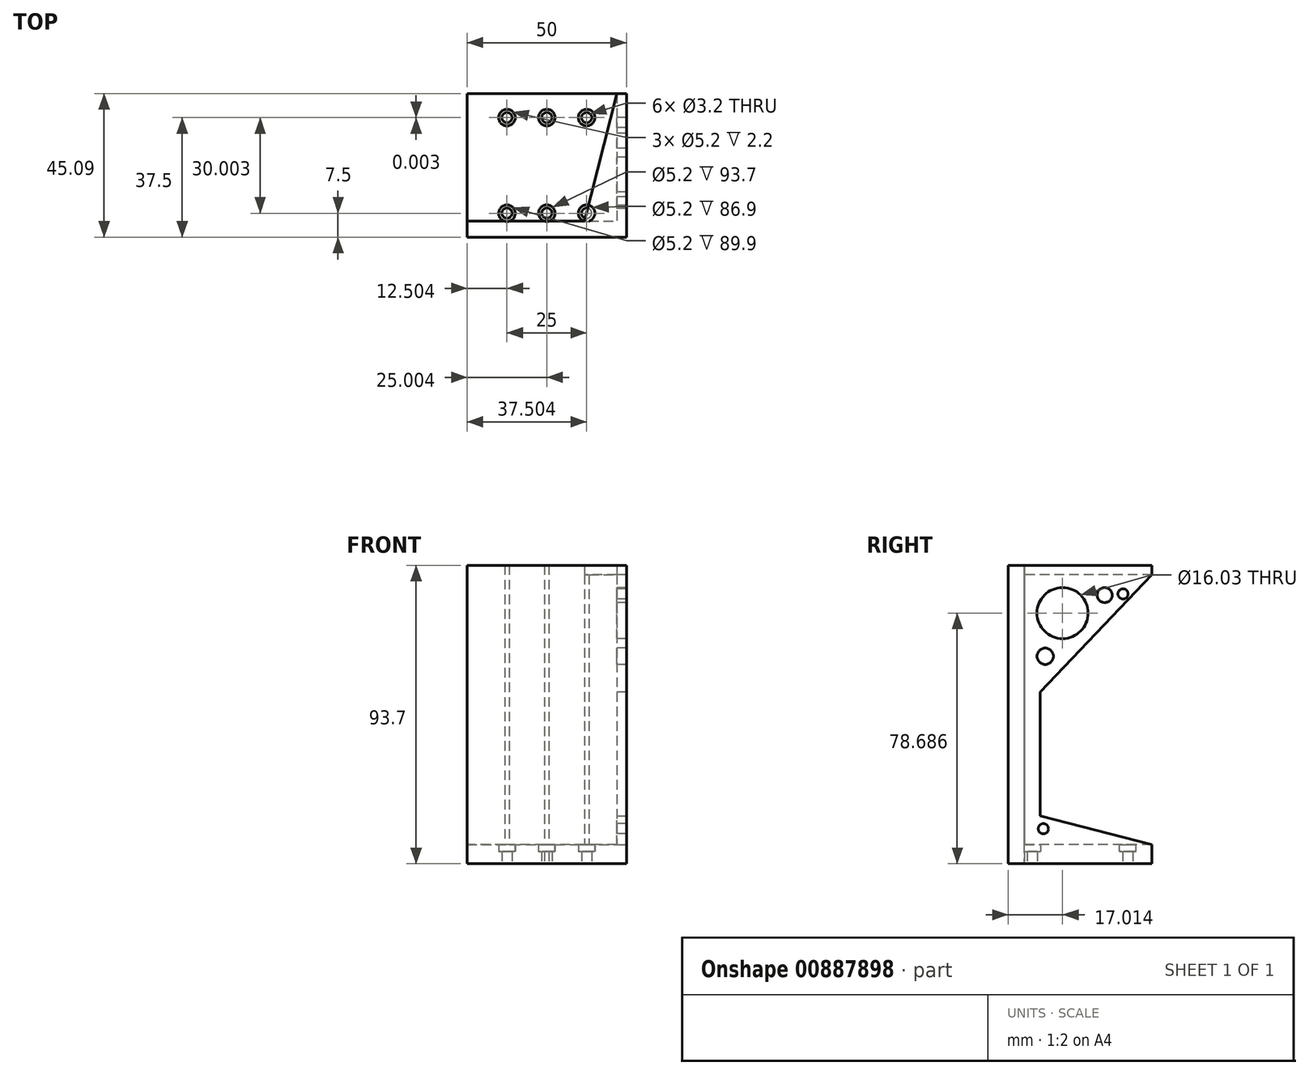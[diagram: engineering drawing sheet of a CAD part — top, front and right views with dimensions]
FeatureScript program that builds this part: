
annotation { "Feature Type Name" : "Feature", "Feature Type Description" : "" }
export const myFeature = defineFeature(function(context is Context, id is Id, definition is map)
    precondition{}
    {
        {
            assignVariable(context, id + "F0", {"name" : "pad", "anyValue" : .2});
        }
        {
            var Q0;
            Q0=qCreatedBy(makeId("Top.planeOp"),FACE);
            var sketch = newSketch(context, id + "F1", { "sketchPlane" : qUnion([Q0])});
            skLineSegment(sketch, "E0.bottom", {"start": v(-37.95, 45) * mm, "end": v(12.05, 45) * mm});
            skLineSegment(sketch, "E0.top", {"start": v(-37.95, 0) * mm, "end": v(12.05, 0) * mm});
            skLineSegment(sketch, "E0.left", {"start": v(-37.95, 45) * mm, "end": v(-37.95, 0) * mm});
            skLineSegment(sketch, "E0.right", {"start": v(12.05, 45) * mm, "end": v(12.05, 0) * mm});
            skLineSegment(sketch, "E1", {"start": v(-37.95, 5) * mm, "end": v(12.05, 5) * mm});
            skLineSegment(sketch, "E2", {"start": v(-37.95, 15) * mm, "end": v(12.05, 15) * mm, "construction": true});
            skLineSegment(sketch, "E3", {"start": v(-37.95, 7.5) * mm, "end": v(12.05, 7.5) * mm, "construction": true});
            skCircle(sketch, "E4", {"center": v(-12.95, 7.5) * mm, "radius": 1.6 * mm});
            skCircle(sketch, "E5", {"center": v(-25.45, 7.5) * mm, "radius": 1.6 * mm});
            skCircle(sketch, "E6", {"center": v(-0.45, 7.5) * mm, "radius": 1.6 * mm});
            skLineSegment(sketch, "E7", {"start": v(9.05, 45) * mm, "end": v(9.05, 0) * mm});
            skCircle(sketch, "E8", {"center": v(-25.45, 7.5) * mm, "radius": 2.6 * mm});
            skCircle(sketch, "E9", {"center": v(-12.95, 7.5) * mm, "radius": 2.6 * mm});
            skCircle(sketch, "E10", {"center": v(-0.45, 7.5) * mm, "radius": 2.6 * mm});
            skLineSegment(sketch, "E11", {"start": v(-37.95, 37.5) * mm, "end": v(12.05, 37.5) * mm, "construction": true});
            skCircle(sketch, "E12", {"center": v(-12.95, 37.5) * mm, "radius": 1.6 * mm});
            skCircle(sketch, "E13", {"center": v(-25.45, 37.5) * mm, "radius": 1.6 * mm});
            skCircle(sketch, "E14", {"center": v(-0.45, 37.5) * mm, "radius": 1.6 * mm});
            skCircle(sketch, "E15", {"center": v(-25.45, 37.5) * mm, "radius": 2.6 * mm});
            skCircle(sketch, "E16", {"center": v(-12.95, 37.5) * mm, "radius": 2.6 * mm});
            skCircle(sketch, "E17", {"center": v(-0.45, 37.5) * mm, "radius": 2.6 * mm});
            skSolve(sketch);
        }
        {
            var Q0;
            {var subQ1=sQuery(id+"F1.wireOp",EDGE,"E0.left");var subQ6=sQuery(id+"F1.wireOp",EDGE,"E0.bottom");var subQ9=makeQuery(id+"F1.imprint","INTERSECT",VERTEX,{"derivedFrom":[subQ6,subQ1]});Q0=makeQuery(id+"F1.imprint","IMPRINT",FACE,{"disambiguationData":[TD([[makeQuery(id+"F1.imprint","IMPRINT",EDGE,{"disambiguationData":[TD([[subQ9,-1.0]])],"derivedFrom":subQ6}),-1.0]])]});}
            var Q1;
            Q1=makeQuery(id+"F1.imprint","IMPRINT",FACE,{"disambiguationData":[TD([[makeQuery(id+"F1.imprint","IMPRINT",EDGE,{"derivedFrom":sQuery(id+"F1.wireOp",EDGE,"E4")}),-1.0]])]});
            var Q2;
            Q2=makeQuery(id+"F1.imprint","IMPRINT",FACE,{"disambiguationData":[TD([[makeQuery(id+"F1.imprint","IMPRINT",EDGE,{"derivedFrom":sQuery(id+"F1.wireOp",EDGE,"E6")}),-1.0]])]});
            var Q3;
            Q3=makeQuery(id+"F1.imprint","IMPRINT",FACE,{"disambiguationData":[TD([[makeQuery(id+"F1.imprint","IMPRINT",EDGE,{"derivedFrom":sQuery(id+"F1.wireOp",EDGE,"E5")}),-1.0]])]});
            var Q4;
            {var subQ0=sQuery(id+"F1.wireOp",EDGE,"E10");var subQ1=sQuery(id+"F1.wireOp",EDGE,"E1");var subQ2=makeQuery(id+"F1.imprint","INTERSECT",VERTEX,{"disambiguationData":[OD(0.0)],"derivedFrom":[subQ1,subQ0]});Q4=makeQuery(id+"F1.imprint","IMPRINT",FACE,{"disambiguationData":[TD([[makeQuery(id+"F1.imprint","IMPRINT",EDGE,{"disambiguationData":[TD([[subQ2,-1.0]])],"derivedFrom":subQ1}),-1.0]])]});}
            var Q5;
            {var subQ0=sQuery(id+"F1.wireOp",EDGE,"E9");var subQ1=sQuery(id+"F1.wireOp",EDGE,"E1");var subQ2=makeQuery(id+"F1.imprint","INTERSECT",VERTEX,{"disambiguationData":[OD(0.0)],"derivedFrom":[subQ1,subQ0]});Q5=makeQuery(id+"F1.imprint","IMPRINT",FACE,{"disambiguationData":[TD([[makeQuery(id+"F1.imprint","IMPRINT",EDGE,{"disambiguationData":[TD([[subQ2,-1.0]])],"derivedFrom":subQ1}),-1.0]])]});}
            var Q6;
            {var subQ0=sQuery(id+"F1.wireOp",EDGE,"E8");var subQ1=sQuery(id+"F1.wireOp",EDGE,"E1");var subQ2=makeQuery(id+"F1.imprint","INTERSECT",VERTEX,{"disambiguationData":[OD(0.0)],"derivedFrom":[subQ1,subQ0]});Q6=makeQuery(id+"F1.imprint","IMPRINT",FACE,{"disambiguationData":[TD([[makeQuery(id+"F1.imprint","IMPRINT",EDGE,{"disambiguationData":[TD([[subQ2,-1.0]])],"derivedFrom":subQ1}),-1.0]])]});}
            var Q7;
            Q7=makeQuery(id+"F1.imprint","IMPRINT",FACE,{"disambiguationData":[TD([[makeQuery(id+"F1.imprint","IMPRINT",EDGE,{"derivedFrom":sQuery(id+"F1.wireOp",EDGE,"E13")}),-1.0]])]});
            var Q8;
            Q8=makeQuery(id+"F1.imprint","IMPRINT",FACE,{"disambiguationData":[TD([[makeQuery(id+"F1.imprint","IMPRINT",EDGE,{"derivedFrom":sQuery(id+"F1.wireOp",EDGE,"E12")}),-1.0]])]});
            var Q9;
            Q9=makeQuery(id+"F1.imprint","IMPRINT",FACE,{"disambiguationData":[TD([[makeQuery(id+"F1.imprint","IMPRINT",EDGE,{"derivedFrom":sQuery(id+"F1.wireOp",EDGE,"E14")}),-1.0]])]});
            extrude(context, id + "F2", {"entities" : qUnion([Q0, Q1, Q2, Q3, Q4, Q5, Q6, Q7, Q8, Q9]), "depth" : (4 + 2) * mm, "offsetDistance" : 25 * mm});
        }
        {
            var Q0;
            {var subQ0=sQuery(id+"F1.wireOp",EDGE,"E0.left");var subQ1=sQuery(id+"F1.wireOp",EDGE,"E0.top");var subQ2=makeQuery(id+"F1.imprint","INTERSECT",VERTEX,{"derivedFrom":[subQ1,subQ0]});Q0=makeQuery(id+"F1.imprint","IMPRINT",FACE,{"disambiguationData":[TD([[makeQuery(id+"F1.imprint","IMPRINT",EDGE,{"disambiguationData":[TD([[subQ2,-1.0]])],"derivedFrom":subQ1}),1.0]])]});}
            var Q1;
            {var subQ0=sQuery(id+"F1.wireOp",EDGE,"E0.right");var subQ1=sQuery(id+"F1.wireOp",EDGE,"E0.top");var subQ2=makeQuery(id+"F1.imprint","INTERSECT",VERTEX,{"derivedFrom":[subQ1,subQ0]});Q1=makeQuery(id+"F1.imprint","IMPRINT",FACE,{"disambiguationData":[TD([[makeQuery(id+"F1.imprint","IMPRINT",EDGE,{"disambiguationData":[TD([[subQ2,1.0]])],"derivedFrom":subQ1}),1.0]])]});}
            var Q2;
            Q2=makeQuery(id+"F2.opExtrude","CAP_FACE",FACE,{"disambiguationData":[OSD([sQuery(id+"F1.wireOp",EDGE,"E0.bottom"),sQuery(id+"F1.wireOp",EDGE,"E0.left"),sQuery(id+"F1.wireOp",EDGE,"E1"),sQuery(id+"F1.wireOp",EDGE,"E4"),sQuery(id+"F1.wireOp",EDGE,"E5"),sQuery(id+"F1.wireOp",EDGE,"E6"),sQuery(id+"F1.wireOp",EDGE,"E7"),sQuery(id+"F1.wireOp",EDGE,"E8"),sQuery(id+"F1.wireOp",EDGE,"E9"),sQuery(id+"F1.wireOp",EDGE,"E10")])],"isStart":false});
            extrude(context, id + "F3", {"entities" : qUnion([Q0, Q1]), "operationType" : NewBodyOperationType.ADD, "endBound" : BoundingType.UP_TO_SURFACE, "depth" : 50 * mm, "endBoundEntityFace" : qUnion([Q2]), "hasOffset" : true, "offsetDistance" : (84.5 + getVariable(context, 'pad')) * mm, "offsetOppositeDirection" : true});
        }
        {
            var Q0;
            {var subQ0=sQuery(id+"F1.wireOp",EDGE,"E0.right");var subQ1=sQuery(id+"F1.wireOp",EDGE,"E0.bottom");var subQ2=makeQuery(id+"F1.imprint","INTERSECT",VERTEX,{"derivedFrom":[subQ1,subQ0]});Q0=makeQuery(id+"F1.imprint","IMPRINT",FACE,{"disambiguationData":[TD([[makeQuery(id+"F1.imprint","IMPRINT",EDGE,{"disambiguationData":[TD([[subQ2,1.0]])],"derivedFrom":subQ1}),-1.0]])]});}
            var Q1;
            Q1=makeQuery(id+"F2.opExtrude","CAP_FACE",FACE,{"disambiguationData":[OSD([sQuery(id+"F1.wireOp",EDGE,"E0.bottom"),sQuery(id+"F1.wireOp",EDGE,"E0.left"),sQuery(id+"F1.wireOp",EDGE,"E1"),sQuery(id+"F1.wireOp",EDGE,"E4"),sQuery(id+"F1.wireOp",EDGE,"E5"),sQuery(id+"F1.wireOp",EDGE,"E6"),sQuery(id+"F1.wireOp",EDGE,"E7")])],"isStart":false});
            extrude(context, id + "F4", {"entities" : qUnion([Q0]), "operationType" : NewBodyOperationType.ADD, "endBound" : BoundingType.UP_TO_SURFACE, "depth" : 25 * mm, "endBoundEntityFace" : qUnion([Q1]), "hasOffset" : true, "offsetDistance" : 9 * mm, "offsetOppositeDirection" : true});
        }
        {
            var Q0;
            Q0=makeQuery(id+"F2.opExtrude","CAP_FACE",FACE,{"disambiguationData":[OSD([sQuery(id+"F1.wireOp",EDGE,"E0.bottom"),sQuery(id+"F1.wireOp",EDGE,"E0.left"),sQuery(id+"F1.wireOp",EDGE,"E1"),sQuery(id+"F1.wireOp",EDGE,"E4"),sQuery(id+"F1.wireOp",EDGE,"E5"),sQuery(id+"F1.wireOp",EDGE,"E6"),sQuery(id+"F1.wireOp",EDGE,"E7")])],"isStart":false});
            var sketch = newSketch(context, id + "F5", { "sketchPlane" : qUnion([Q0])});
            skCircle(sketch, "E18.0", {"center": v(-25.45, 7.5) * mm, "radius": 2.6 * mm});
            skCircle(sketch, "E19.0", {"center": v(-12.95, 7.5) * mm, "radius": 2.6 * mm});
            skCircle(sketch, "E20.0", {"center": v(-0.45, 7.5) * mm, "radius": 2.6 * mm});
            skCircle(sketch, "E21.0", {"center": v(-25.45, 37.5) * mm, "radius": 2.6 * mm});
            skCircle(sketch, "E22.0", {"center": v(-12.95, 37.5) * mm, "radius": 2.6 * mm});
            skCircle(sketch, "E23.0", {"center": v(-0.45, 37.5) * mm, "radius": 2.6 * mm});
            skSolve(sketch);
        }
        {
            var Q0;
            {var subQ7=sQuery(id+"F1.wireOp",EDGE,"E5");Q0=makeQuery(id+"F5.imprint","IMPRINT",FACE,{"disambiguationData":[TD([[makeQuery(id+"F5.imprint","IMPRINT",EDGE,{"derivedFrom":makeQuery(id+"F2.opExtrude","CAP_EDGE",EDGE,{"disambiguationData":[OSD([subQ7])],"isStart":false})}),-1.0]])]});}
            var Q1;
            {var subQ6=sQuery(id+"F1.wireOp",EDGE,"E4");Q1=makeQuery(id+"F5.imprint","IMPRINT",FACE,{"disambiguationData":[TD([[makeQuery(id+"F5.imprint","IMPRINT",EDGE,{"derivedFrom":makeQuery(id+"F2.opExtrude","CAP_EDGE",EDGE,{"disambiguationData":[OSD([subQ6])],"isStart":false})}),-1.0]])]});}
            var Q2;
            {var subQ8=sQuery(id+"F1.wireOp",EDGE,"E6");Q2=makeQuery(id+"F5.imprint","IMPRINT",FACE,{"disambiguationData":[TD([[makeQuery(id+"F5.imprint","IMPRINT",EDGE,{"derivedFrom":makeQuery(id+"F2.opExtrude","CAP_EDGE",EDGE,{"disambiguationData":[OSD([subQ8])],"isStart":false})}),-1.0]])]});}
            var Q3;
            Q3=makeQuery(id+"F5.imprint","IMPRINT",FACE,{"disambiguationData":[TD([[makeQuery(id+"F5.imprint","IMPRINT",EDGE,{"derivedFrom":sQuery(id+"F5.wireOp",EDGE,"E21.0")}),1.0]])]});
            var Q4;
            Q4=makeQuery(id+"F5.imprint","IMPRINT",FACE,{"disambiguationData":[TD([[makeQuery(id+"F5.imprint","IMPRINT",EDGE,{"derivedFrom":sQuery(id+"F5.wireOp",EDGE,"E22.0")}),1.0]])]});
            var Q5;
            Q5=makeQuery(id+"F5.imprint","IMPRINT",FACE,{"disambiguationData":[TD([[makeQuery(id+"F5.imprint","IMPRINT",EDGE,{"derivedFrom":sQuery(id+"F5.wireOp",EDGE,"E23.0")}),1.0]])]});
            extrude(context, id + "F6", {"entities" : qUnion([Q0, Q1, Q2, Q3, Q4, Q5]), "operationType" : NewBodyOperationType.REMOVE, "oppositeDirection" : true, "depth" : (2 + getVariable(context, 'pad')) * mm, "offsetDistance" : 25 * mm});
        }
        {
            var Q0;
            Q0=makeQuery(id+"F4.opExtrude","CAP_FACE",FACE,{"disambiguationData":[OSD([sQuery(id+"F1.wireOp",EDGE,"E0.bottom"),sQuery(id+"F1.wireOp",EDGE,"E0.right"),sQuery(id+"F1.wireOp",EDGE,"E1"),sQuery(id+"F1.wireOp",EDGE,"E7")])],"isStart":false});
            var sketch = newSketch(context, id + "F7", { "sketchPlane" : qUnion([Q0])});
            skLineSegment(sketch, "E24", {"start": v(9.05, 10) * mm, "end": v(12.05, 10) * mm});
            skSolve(sketch);
        }
        {
            var Q0;
            {var subQ0=sQuery(id+"F7.wireOp",EDGE,"E24");Q0=makeQuery(id+"F7.imprint","IMPRINT",FACE,{"disambiguationData":[TD([[makeQuery(id+"F7.imprint","IMPRINT",EDGE,{"derivedFrom":subQ0}),-1.0]])]});}
            var Q1;
            Q1=makeQuery(id+"F3.opExtrude","CAP_FACE",FACE,{"disambiguationData":[OSD([sQuery(id+"F1.wireOp",EDGE,"E0.top"),sQuery(id+"F1.wireOp",EDGE,"E0.left"),sQuery(id+"F1.wireOp",EDGE,"E0.right"),sQuery(id+"F1.wireOp",EDGE,"E1"),sQuery(id+"F1.wireOp",EDGE,"E8"),sQuery(id+"F1.wireOp",EDGE,"E9"),sQuery(id+"F1.wireOp",EDGE,"E10")])],"isStart":false});
            extrude(context, id + "F8", {"entities" : qUnion([Q0]), "operationType" : NewBodyOperationType.ADD, "endBound" : BoundingType.UP_TO_SURFACE, "depth" : 25 * mm, "endBoundEntityFace" : qUnion([Q1]), "offsetDistance" : 25 * mm});
        }
        {
            var Q0;
            {var subQ0=sQuery(id+"F1.wireOp",EDGE,"E7");Q0=makeQuery(id+"F8.boolean.opBoolean","MERGE",FACE,{"derivedFrom":[makeQuery(id+"F4.opExtrude","SWEPT_FACE",FACE,{"disambiguationData":[OSD([subQ0])]}),makeQuery(id+"F8.opExtrude","SWEPT_FACE",FACE,{"disambiguationData":[OSD([subQ0])]})]});}
            var sketch = newSketch(context, id + "F9", { "sketchPlane" : qUnion([Q0])});
            skLineSegment(sketch, "E25", {"start": v(-45.1, 90.7) * mm, "end": v(-5, 48.7) * mm});
            skLineSegment(sketch, "E26", {"start": v(-45.1, 90.7) * mm, "end": v(-5, 90.7) * mm});
            skSolve(sketch);
        }
        {
            var Q0;
            {var subQ0=sQuery(id+"F9.wireOp",EDGE,"E26");var subQ1=sQuery(id+"F9.wireOp",EDGE,"E25");var subQ2=makeQuery(id+"F9.imprint","INTERSECT",VERTEX,{"derivedFrom":[subQ1,subQ0]});Q0=makeQuery(id+"F9.imprint","IMPRINT",FACE,{"disambiguationData":[TD([[makeQuery(id+"F9.imprint","IMPRINT",EDGE,{"disambiguationData":[TD([[subQ2,-1.0]])],"derivedFrom":subQ1}),1.0]])]});}
            var Q1;
            {var subQ0=sQuery(id+"F1.wireOp",EDGE,"E0.right");Q1=makeQuery(id+"F12.boolean.opBoolean","MERGE",FACE,{"derivedFrom":[makeQuery(id+"F8.boolean.opBoolean","MERGE",FACE,{"derivedFrom":[makeQuery(id+"F4.boolean.opBoolean","MERGE",FACE,{"derivedFrom":[makeQuery(id+"F3.opExtrude","SWEPT_FACE",FACE,{"disambiguationData":[OSD([subQ0])]}),makeQuery(id+"F4.opExtrude","SWEPT_FACE",FACE,{"disambiguationData":[OSD([subQ0])]})]}),makeQuery(id+"F8.opExtrude","SWEPT_FACE",FACE,{"disambiguationData":[OSD([subQ0])]})]}),makeQuery(id+"F12.opExtrude","SWEPT_FACE",FACE,{"disambiguationData":[OSD([subQ0])]})]});}
            extrude(context, id + "F10", {"entities" : qUnion([Q0]), "operationType" : NewBodyOperationType.ADD, "endBound" : BoundingType.UP_TO_SURFACE, "oppositeDirection" : true, "depth" : 25 * mm, "endBoundEntityFace" : qUnion([Q1]), "offsetDistance" : 25 * mm});
        }
        {
            var Q0;
            {var subQ0=sQuery(id+"F1.wireOp",EDGE,"E1");var subQ1=sQuery(id+"F1.wireOp",EDGE,"E0.right");Q0=makeQuery(id+"F8.boolean.opBoolean","MERGE",FACE,{"derivedFrom":[makeQuery(id+"F3.opExtrude","CAP_FACE",FACE,{"disambiguationData":[OSD([sQuery(id+"F1.wireOp",EDGE,"E0.top"),sQuery(id+"F1.wireOp",EDGE,"E0.left"),subQ1,subQ0,sQuery(id+"F1.wireOp",EDGE,"E8"),sQuery(id+"F1.wireOp",EDGE,"E9"),sQuery(id+"F1.wireOp",EDGE,"E10")])],"isStart":false}),makeQuery(id+"F8.opExtrude","CAP_FACE",FACE,{"disambiguationData":[OSD([subQ1,subQ0,sQuery(id+"F1.wireOp",EDGE,"E7"),sQuery(id+"F7.wireOp",EDGE,"E24")])],"isStart":false})]});}
            var sketch = newSketch(context, id + "F11", { "sketchPlane" : qUnion([Q0])});
            skLineSegment(sketch, "E27", {"start": v(9.05, 45.1) * mm, "end": v(-1.16, 5) * mm});
            skSolve(sketch);
        }
        {
            var Q0;
            {var subQ3=sQuery(id+"F11.wireOp",EDGE,"8G0JBkG0-ZzZr-AH65-pQjR-1Y3BWd0RR8ZH");Q0=makeQuery(id+"F11.imprint","IMPRINT",FACE,{"disambiguationData":[TD([[makeQuery(id+"F11.imprint","IMPRINT",EDGE,{"derivedFrom":subQ3}),1.0]])]});}
            var Q1;
            Q1=makeQuery(id+"F11.imprint","IMPRINT",FACE,{"disambiguationData":[TD([[makeQuery(id+"F11.imprint","IMPRINT",EDGE,{"derivedFrom":sQuery(id+"F11.wireOp",EDGE,"E27")}),1.0]])]});
            var Q2;
            Q2=makeQuery(id+"F11.imprint","IMPRINT",FACE,{"disambiguationData":[TD([[makeQuery(id+"F11.imprint","IMPRINT",EDGE,{"derivedFrom":makeQuery(id+"F3.opExtrude","CAP_EDGE",EDGE,{"disambiguationData":[OSD([sQuery(id+"F1.wireOp",EDGE,"E0.top")])],"isStart":false})}),1.0]])]});
            extrude(context, id + "F12", {"entities" : qUnion([Q0, Q1, Q2]), "operationType" : NewBodyOperationType.ADD, "depth" : 3 * mm, "offsetDistance" : 25 * mm});
        }
        {
            var Q0;
            {var subQ0=sQuery(id+"F1.wireOp",EDGE,"E7");Q0=makeQuery(id+"F10.boolean.opBoolean","MERGE",FACE,{"derivedFrom":[makeQuery(id+"F8.boolean.opBoolean","MERGE",FACE,{"derivedFrom":[makeQuery(id+"F4.opExtrude","SWEPT_FACE",FACE,{"disambiguationData":[OSD([subQ0])]}),makeQuery(id+"F8.opExtrude","SWEPT_FACE",FACE,{"disambiguationData":[OSD([subQ0])]})]}),makeQuery(id+"F10.opExtrude","CAP_FACE",FACE,{"disambiguationData":[OSD([subQ0,sQuery(id+"F7.wireOp",EDGE,"E24"),sQuery(id+"F9.wireOp",EDGE,"E25"),sQuery(id+"F9.wireOp",EDGE,"E26")])],"isStart":true})]});}
            var sketch = newSketch(context, id + "F13", { "sketchPlane" : qUnion([Q0])});
            skCircle(sketch, "E28", {"center": v(-11, 11) * mm, "radius": 1.6 * mm});
            skCircle(sketch, "E29", {"center": v(-36, 84.7) * mm, "radius": 1.6 * mm});
            skCircle(sketch, "E30", {"center": v(-11.58, 65.13) * mm, "radius": 2.58 * mm});
            skCircle(sketch, "E31", {"center": v(-17.01, 78.69) * mm, "radius": 8.01 * mm});
            skLineSegment(sketch, "E32", {"start": v(-25.51, 70.19) * mm, "end": v(-5, 90.7) * mm, "construction": true});
            skCircle(sketch, "E33", {"center": v(-30.23, 84.34) * mm, "radius": 2.36 * mm});
            skSolve(sketch);
        }
        {
            var Q0;
            Q0=makeQuery(id+"F13.imprint","IMPRINT",FACE,{"disambiguationData":[TD([[makeQuery(id+"F13.imprint","IMPRINT",EDGE,{"derivedFrom":sQuery(id+"F13.wireOp",EDGE,"E29")}),1.0]])]});
            var Q1;
            Q1=makeQuery(id+"F13.imprint","IMPRINT",FACE,{"disambiguationData":[TD([[makeQuery(id+"F13.imprint","IMPRINT",EDGE,{"derivedFrom":sQuery(id+"F13.wireOp",EDGE,"E31")}),1.0]])]});
            var Q2;
            Q2=makeQuery(id+"F13.imprint","IMPRINT",FACE,{"disambiguationData":[TD([[makeQuery(id+"F13.imprint","IMPRINT",EDGE,{"derivedFrom":sQuery(id+"F13.wireOp",EDGE,"E30")}),1.0]])]});
            var Q3;
            Q3=makeQuery(id+"F13.imprint","IMPRINT",FACE,{"disambiguationData":[TD([[makeQuery(id+"F13.imprint","IMPRINT",EDGE,{"derivedFrom":sQuery(id+"F13.wireOp",EDGE,"E33")}),1.0]])]});
            var Q4;
            Q4=makeQuery(id+"F13.imprint","IMPRINT",FACE,{"disambiguationData":[TD([[makeQuery(id+"F13.imprint","IMPRINT",EDGE,{"derivedFrom":sQuery(id+"F13.wireOp",EDGE,"E28")}),1.0]])]});
            var Q5;
            {var subQ0=sQuery(id+"F9.wireOp",EDGE,"E26");var subQ1=sQuery(id+"F1.wireOp",EDGE,"E0.right");Q5=makeQuery(id+"F12.boolean.opBoolean","MERGE",FACE,{"derivedFrom":[makeQuery(id+"F10.boolean.opBoolean","MERGE",FACE,{"derivedFrom":[makeQuery(id+"F8.boolean.opBoolean","MERGE",FACE,{"derivedFrom":[makeQuery(id+"F4.boolean.opBoolean","MERGE",FACE,{"derivedFrom":[makeQuery(id+"F3.opExtrude","SWEPT_FACE",FACE,{"disambiguationData":[OSD([subQ1])]}),makeQuery(id+"F4.opExtrude","SWEPT_FACE",FACE,{"disambiguationData":[OSD([subQ1])]})]}),makeQuery(id+"F8.opExtrude","SWEPT_FACE",FACE,{"disambiguationData":[OSD([subQ1])]})]}),makeQuery(id+"F10.opExtrude","CAP_FACE",FACE,{"disambiguationData":[OSD([sQuery(id+"F1.wireOp",EDGE,"E7"),sQuery(id+"F7.wireOp",EDGE,"E24"),sQuery(id+"F9.wireOp",EDGE,"E25"),subQ0])],"isStart":false})]}),makeQuery(id+"F12.opExtrude","SWEPT_FACE",FACE,{"disambiguationData":[OSD([subQ1,subQ0])]})]});}
            extrude(context, id + "F14", {"entities" : qUnion([Q0, Q1, Q2, Q3, Q4]), "operationType" : NewBodyOperationType.REMOVE, "endBound" : BoundingType.UP_TO_SURFACE, "oppositeDirection" : true, "depth" : 25 * mm, "endBoundEntityFace" : qUnion([Q5]), "offsetDistance" : 25 * mm});
        }
        {
            var Q0;
            Q0=makeQuery(id+"F4.opExtrude","CAP_EDGE",EDGE,{"disambiguationData":[OSD([sQuery(id+"F1.wireOp",EDGE,"E0.bottom")])],"isStart":false});
            chamfer(context, id + "F15", {"entities" : qUnion([Q0]), "chamferType" : ChamferType.TWO_OFFSETS, "width1" : 9 * mm, "oppositeDirection" : false, "width2" : 35 * mm, "tangentPropagation" : true});
        }
    });
